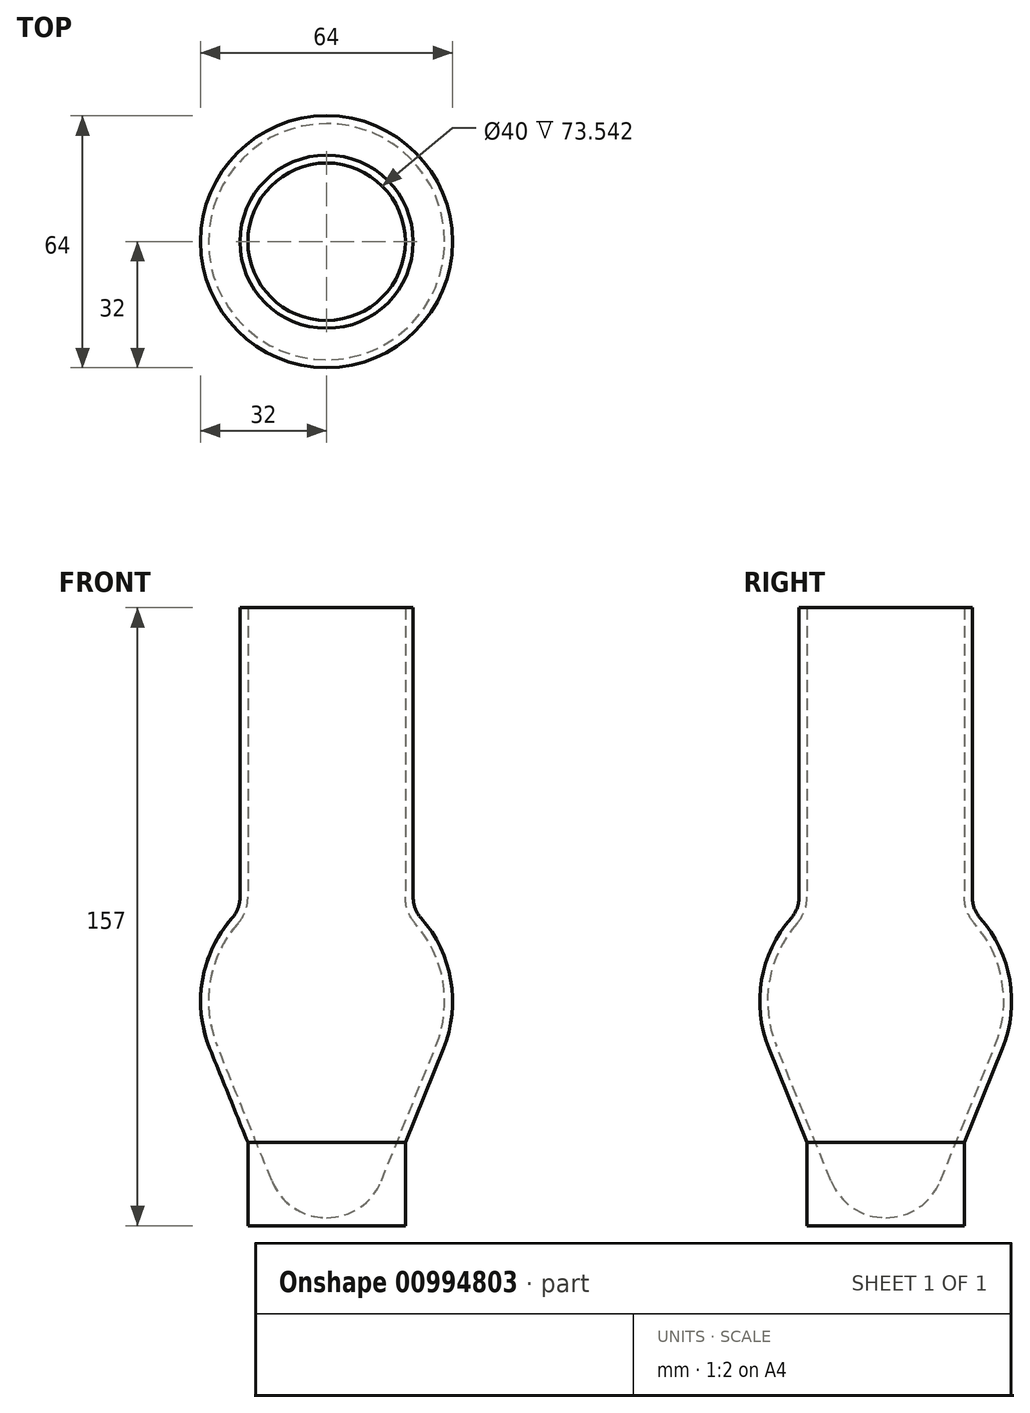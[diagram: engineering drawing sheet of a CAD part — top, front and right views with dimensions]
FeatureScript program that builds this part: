
annotation { "Feature Type Name" : "Feature", "Feature Type Description" : "" }
export const myFeature = defineFeature(function(context is Context, id is Id, definition is map)
    precondition{}
    {
        {
            var Q0;
            Q0=qCreatedBy(makeId("Front.planeOp"),FACE);
            var sketch = newSketch(context, id + "F0", { "sketchPlane" : qUnion([Q0])});
            skArc(sketch, "E0", {"start": v(27.81, -11.25) * mm, "mid": v(29.57, 5.05) * mm, "end": v(22.5, 19.84) * mm});
            skLineSegment(sketch, "E1", {"start": v(20, 100) * mm, "end": v(20, 26.46) * mm});
            skArc(sketch, "E2", {"start": v(0, -55) * mm, "mid": v(8.39, -52.44) * mm, "end": v(13.9, -45.62) * mm});
            skLineSegment(sketch, "E3", {"start": v(27.81, -11.25) * mm, "end": v(13.9, -45.63) * mm});
            skPoint(sketch, "E4.orphan", {"position": v(20, 0) * mm});
            skLineSegment(sketch, "E5", {"start": v(0, -55) * mm, "end": v(0, -57) * mm});
            skLineSegment(sketch, "E6", {"start": v(0, -57) * mm, "end": v(20, -57) * mm});
            skPoint(sketch, "E7.orphan", {"position": v(0, -51) * mm});
            skPoint(sketch, "E8.visualSharp", {"position": v(20, 22.36) * mm});
            skArc(sketch, "E8.filletArc", {"start": v(20, 26.46) * mm, "mid": v(20.65, 22.92) * mm, "end": v(22.5, 19.84) * mm});
            skLineSegment(sketch, "E9.0", {"start": v(22, 100) * mm, "end": v(22, 26.46) * mm});
            skArc(sketch, "E9.1", {"start": v(22, 26.46) * mm, "mid": v(22.52, 23.63) * mm, "end": v(24, 21.17) * mm});
            skArc(sketch, "E9.2", {"start": v(29.66, -12) * mm, "mid": v(31.54, 5.39) * mm, "end": v(24, 21.17) * mm});
            skLineSegment(sketch, "E9.3", {"start": v(29.66, -12) * mm, "end": v(20, -35.9) * mm});
            skLineSegment(sketch, "E10", {"start": v(20, 100) * mm, "end": v(22, 100) * mm});
            skLineSegment(sketch, "E11", {"start": v(20, -57) * mm, "end": v(20, -35.9) * mm});
            skLineSegment(sketch, "E12", {"start": v(0, 0) * mm, "end": v(0, 111.14) * mm});
            skSolve(sketch);
        }
        {
            var Q0;
            Q0 = qSketchRegion(id + "F0", true);
            var Q1;
            Q1=sQuery(id+"F0.wireOp",EDGE,"E12");
            revolve(context, id + "F1", {"surfaceOperationType" : NewSurfaceOperationType.NEW, "entities" : qUnion([Q0]), "axis" : qUnion([Q1]), "revolveType" : RevolveType.FULL});
        }
    });
